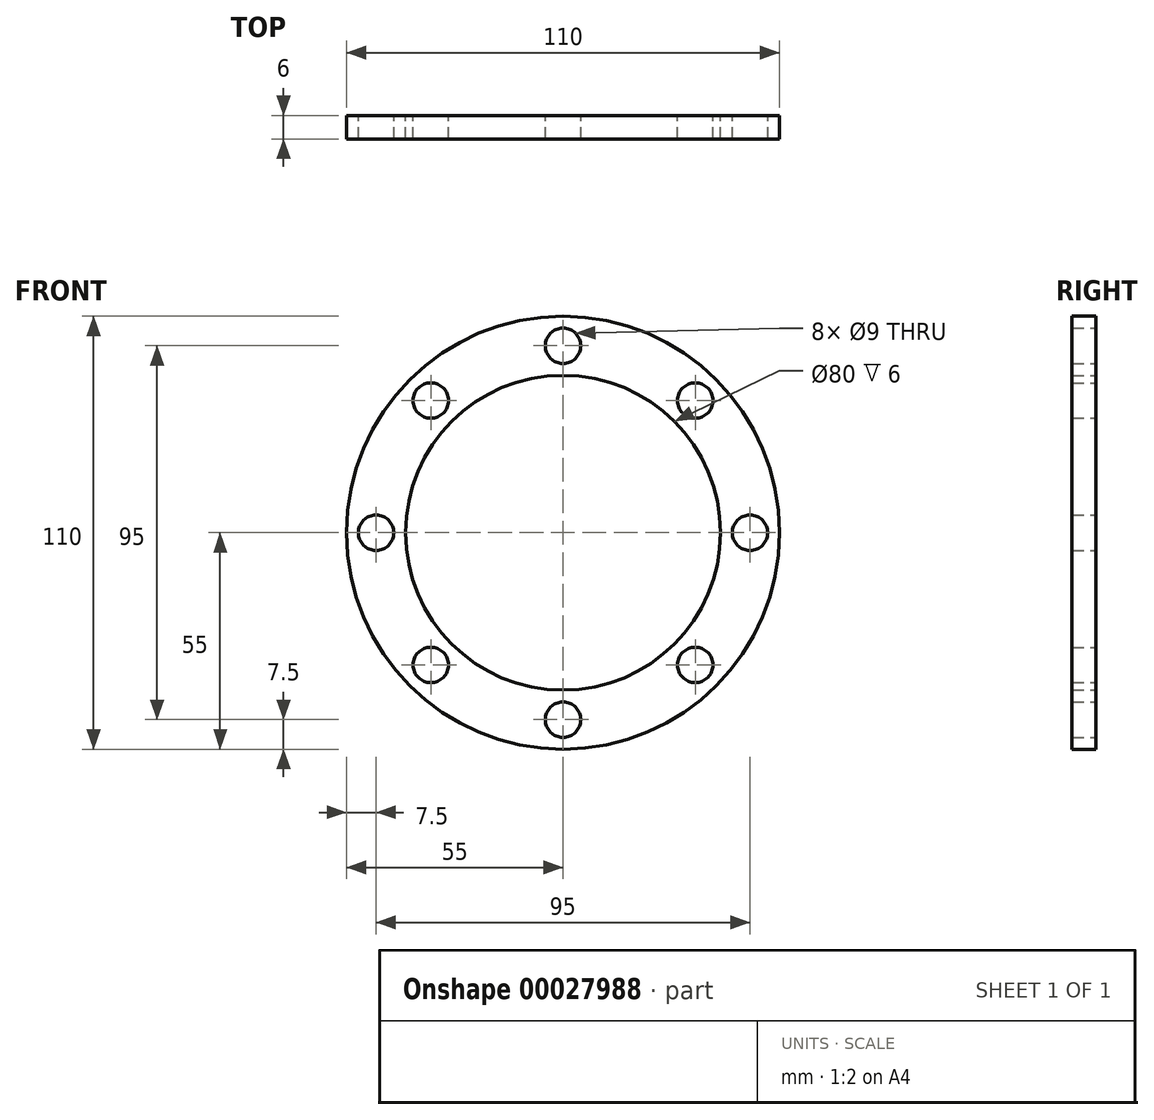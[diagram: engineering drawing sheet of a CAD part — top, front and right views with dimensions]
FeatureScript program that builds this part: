
annotation { "Feature Type Name" : "Feature", "Feature Type Description" : "" }
export const myFeature = defineFeature(function(context is Context, id is Id, definition is map)
    precondition{}
    {
        {
            var Q0;
            Q0=qCreatedBy(makeId("Front.planeOp"),FACE);
            var sketch = newSketch(context, id + "F0", { "sketchPlane" : qUnion([Q0])});
            skCircle(sketch, "E0", {"center": v(0, 0) * mm, "radius": 55 * mm});
            skCircle(sketch, "E1", {"center": v(0, 47.5) * mm, "radius": 4.5 * mm});
            skCircle(sketch, "E2", {"center": v(0, 0) * mm, "radius": 40 * mm});
            skCircle(sketch, "E3.1.0", {"center": v(-33.59, 33.59) * mm, "radius": 4.5 * mm});
            skCircle(sketch, "E3.2.0", {"center": v(-47.5, 0) * mm, "radius": 4.5 * mm});
            skCircle(sketch, "E4.1.3.0", {"center": v(-33.59, -33.59) * mm, "radius": 4.5 * mm});
            skCircle(sketch, "E4.1.4.0", {"center": v(0, -47.5) * mm, "radius": 4.5 * mm});
            skCircle(sketch, "E4.1.5.0", {"center": v(33.59, -33.59) * mm, "radius": 4.5 * mm});
            skCircle(sketch, "E4.1.6.0", {"center": v(47.5, 0) * mm, "radius": 4.5 * mm});
            skCircle(sketch, "E4.1.7.0", {"center": v(33.59, 33.59) * mm, "radius": 4.5 * mm});
            skSolve(sketch);
        }
        {
            var Q0;
            Q0=makeQuery(id+"F0.imprint","IMPRINT",FACE,{"disambiguationData":[TD([[makeQuery(id+"F0.imprint","IMPRINT",EDGE,{"derivedFrom":sQuery(id+"F0.wireOp",EDGE,"E0")}),1.0]])]});
            extrude(context, id + "F1", {"entities" : qUnion([Q0]), "depth" : 6 * mm});
        }
    });
